# Revit family: Domotics-DomesticRanges-GEWISS-27COMBI_SYSTEM-IP40_SOCKET-OUTLET_DEU
name_source: partatom
category: Apparecchi elettrici
revit_build: Autodesk Revit 2016 (Build: 20161004_0715(x64)
units: mm (PartAtom-declared; Revit-internal decimal feet)

## family parameters
Condiviso = No
Host = Superficie
Mantenere orientamento annotazione = Sì
Punto di calcolo locali = Sì
Quota connettore circolare = Usa diametro
Taglio con vuoti quando caricato = No
Tipo di parte = Normale

## types (1)
- Domotics-DomesticRanges-GEWISS-27COMBI_SYSTEM-IP40_SOCKET-OUTLET_DEU
    Carico apparente = 0 VA
    Catalogue = DOMOTICS
    Catalogue Range = 27COMBI
    Characteristics = German standard
    Colour = Grey RAL 7035
    Description: = Socket-outlet 2P+E - 16A
    Descrizione = 2P+E 16A GER STD SOCKET IP40
    EAN code = 8011564095427
    Electrocod = 0131
    Glow Wire Test = 650°C
    IDF = cc79028c-f698-4933-8984-bee1ec4ebd57
    IDT = d2cc88c2-2bd0-4b6a-a7a0-6ff77e855ea8
    IP degree = IP40
    Immagine tipo = GW27814.jpg
    Installation temperature = -25 +60 °C
    Insulation class = II
    Lid screws = Corrosion-resistant steel
    Modello = GW27814
    N. holes Ã˜ 23 with cable gland = 1
    N. poli = 1
    No. knockout holes Ã˜23 = 3 on sides / 1 on the bottom
    Outer dim. LxHxD (mm) = 66x82x55
    Produttore = GEWISS S.p.A.
    Prospetto di default = 1219 mm
    SEO = Enclosure
    Standard = IEC 60884-1
    Standard; = IEC 60884-1
    TXT ELETTRICO = 16
    Technical sheet = https://www.gewiss.com
    Thermo-pressure with ball = 70
    Torque screws tightening = 0,8NM
    Type of knockout holes = Removable with tool
    URL = https://www.gewiss.com
    Version file RFA = 19.4
    Volt = 230 V
    Voltage = 250 V ac
    Voltage: = 250 V ac

note: source unit labels omitted for Thermo-pressure with ball — the stored unit's dimension contradicts the parameter name (converter mislabeling)

## geometry (parser evidence)
native form markers: Sweep x1
no freeform markers — native parametric forms only
